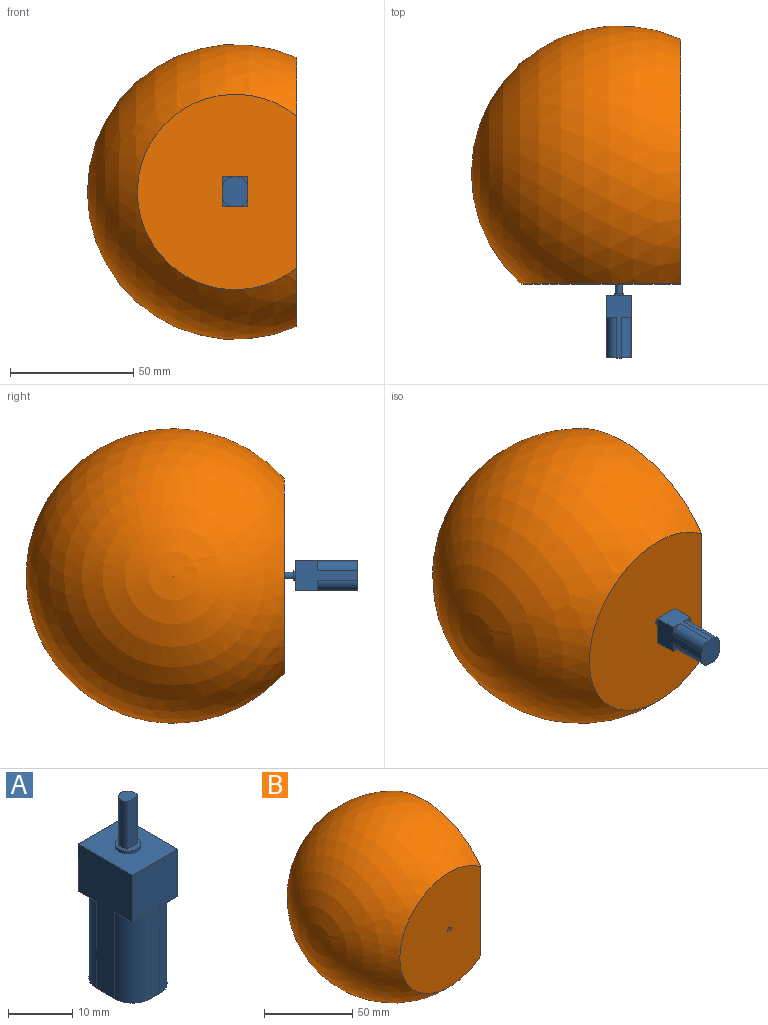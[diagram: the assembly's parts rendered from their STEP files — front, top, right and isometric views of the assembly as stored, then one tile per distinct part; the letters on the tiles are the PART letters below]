
ASSEMBLY  parts=2 mates=1
PART A: 19 faces, bbox 10x12x35.1 mm
  f0: plane 2.95x2.45mm, normal (0,0,1), area 6.1mm2, adj f17,f18
  f1: plane 25.5x12mm, normal (1,0,0), area 174mm2, adj f2,f4,f5,f6,f9,f10,f13,f14
  f2: plane 25.5x10mm, normal (0,1,0), area 123mm2, adj f1,f3,f5,f6,f7,f10,f11,f13
  f3: plane 25.5x12mm, normal (-1,0,0), area 174mm2, adj f2,f4,f5,f7,f8,f11,f12,f13
  f4: plane 25.5x10mm, normal (0,-1,0), area 123mm2, adj f1,f3,f5,f8,f9,f12,f13,f14
  f5: plane 12x10mm, normal (0,0,-1), area 106.3mm2, adj f1,f2,f3,f4,f6,f7,f8,f9
  f6: cylinder r=4mm len=16.5mm, axis (0,0,1), area 103.7mm2, adj f1,f2,f5,f10
  f7: cylinder r=4mm len=16.5mm, axis (0,0,-1), area 103.7mm2, adj f2,f3,f5,f11
  f8: cylinder r=4mm len=16.5mm, axis (0,0,1), area 103.7mm2, adj f3,f4,f5,f12
  f9: cylinder r=4mm len=16.5mm, axis (0,0,-1), area 103.7mm2, adj f1,f4,f5,f14
  f10: plane 4x4mm, normal (0,0,-1), area 3.4mm2, adj f1,f2,f6
  f11: plane 4x4mm, normal (0,0,-1), area 3.4mm2, adj f2,f3,f7
  f12: plane 4x4mm, normal (0,0,-1), area 3.4mm2, adj f3,f4,f8
  f13: plane 12x10mm, normal (0,0,1), area 107.4mm2, adj f1,f2,f3,f4,f15
  f14: plane 4x4mm, normal (0,0,-1), area 3.4mm2, adj f1,f4,f9
  f15: cylinder r=2mm len=4mm, axis (0,0,-1), area 6.9mm2, adj f13,f16
  f16: plane 4x4mm, normal (0,0,1), area 6.5mm2, adj f15,f17,f18
  f17: cylinder r=1.47mm len=9mm, axis (0,0,-1), area 60.9mm2, adj f0,f16,f18
  f18: plane 9x2.21mm, normal (0,-1,0), area 19.9mm2, adj f0,f16,f17
PART B: 10 faces, bbox 85x120x120 mm
  f0: sphere r=55mm, area 19717.1mm2, adj f2,f4,f5,f8,f9
  f1: sphere r=60mm, area 27160.3mm2, adj f2,f3
  f2: plane 109.09x99.54mm, normal (1,0,0), area 1752.6mm2, adj f0,f1,f3,f8
  f3: plane 79.37x64.69mm, normal (0,-1,0), area 4311.8mm2, adj f1,f2,f6,f7
  f4: plane 21.47x10.23mm, normal (-0.9,0,-0.43), area 27.6mm2, adj f0,f8
  f5: plane 21.47x10.23mm, normal (-0.9,0,0.43), area 27.6mm2, adj f0,f8
  f6: cylinder r=1.47mm len=5mm, axis (0,-1,0), area 33.8mm2, adj f3,f7,f8
  f7: plane 5x2.21mm, normal (0,0,1), area 11.1mm2, adj f3,f6,f8
  f8: plane 75.5x62.75mm, normal (0,1,0), area 3909.6mm2, adj f0,f2,f4,f5,f6,f7
  f9: plane 63.25x63.25mm, normal (1,0,0), area 3141.6mm2, adj f0
PLACE A rot(axis=(0,0.71,0.71),180deg) t=(0,-75.05,0.12)mm
PLACE B at identity
MATE fastened A.f17 <-> B.f8  axis (0,1,0) through (0,-40,0.12)mm
